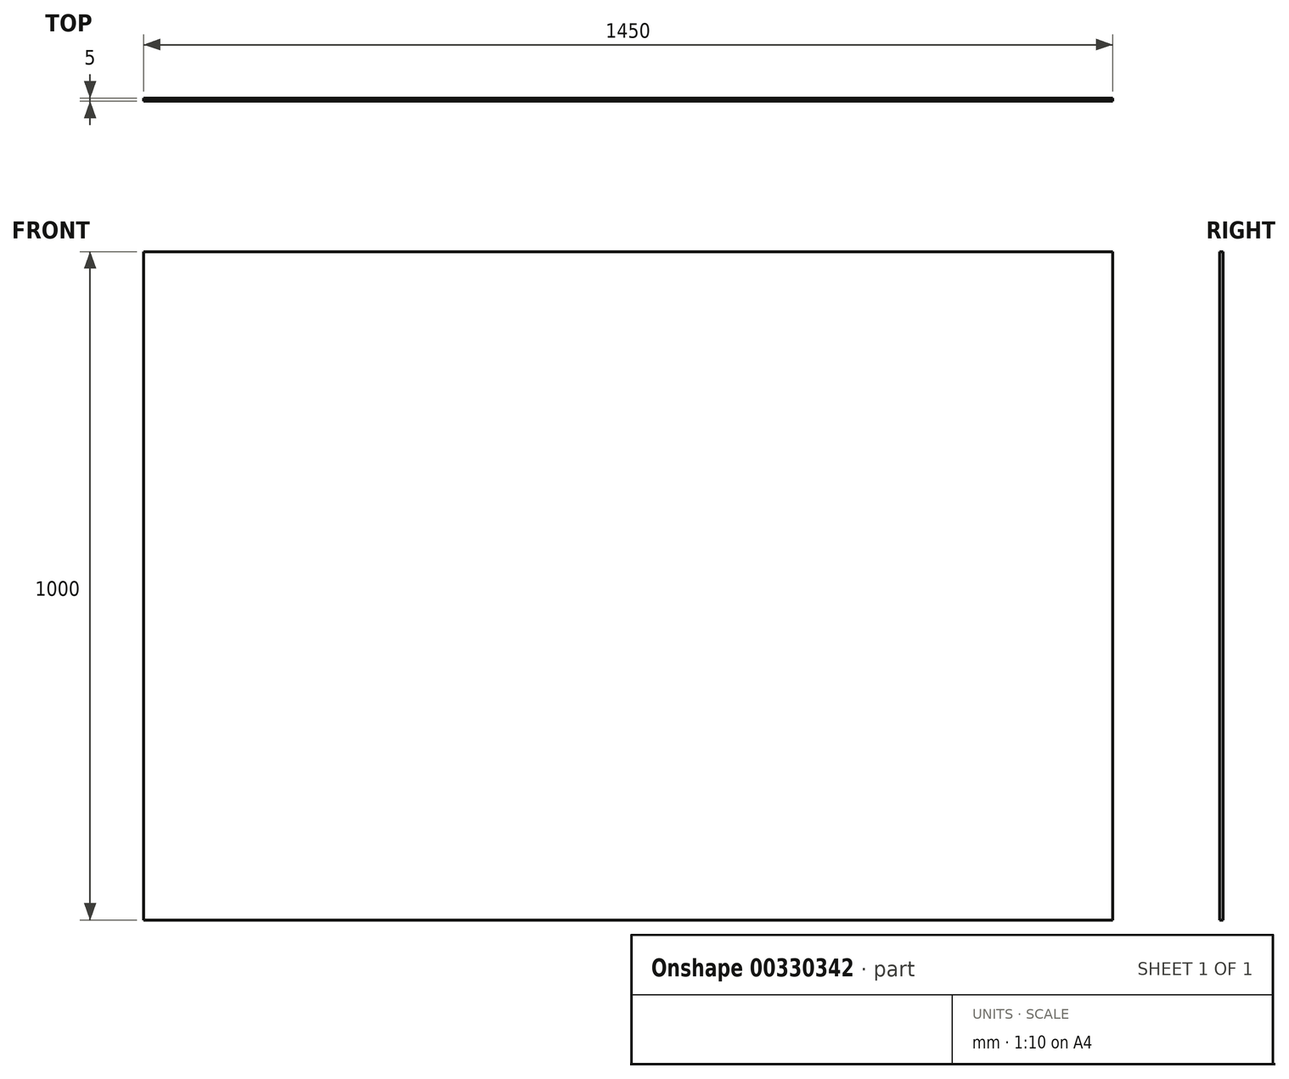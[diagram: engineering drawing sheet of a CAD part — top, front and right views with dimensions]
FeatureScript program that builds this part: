
annotation { "Feature Type Name" : "Feature", "Feature Type Description" : "" }
export const myFeature = defineFeature(function(context is Context, id is Id, definition is map)
    precondition{}
    {
        {
            var Q0;
            Q0=qCreatedBy(makeId("Front.planeOp"),FACE);
            var sketch = newSketch(context, id + "F0", { "sketchPlane" : qUnion([Q0])});
            skLineSegment(sketch, "E0.bottom", {"start": v(0, 0) * mm, "end": v(1450, 0) * mm});
            skLineSegment(sketch, "E0.top", {"start": v(0, 1000) * mm, "end": v(1450, 1000) * mm});
            skLineSegment(sketch, "E0.left", {"start": v(0, 0) * mm, "end": v(0, 1000) * mm});
            skLineSegment(sketch, "E0.right", {"start": v(1450, 0) * mm, "end": v(1450, 1000) * mm});
            skSolve(sketch);
        }
        {
            var Q0;
            Q0 = qSketchRegion(id + "F0", true);
            extrude(context, id + "F1", {"entities" : qUnion([Q0]), "depth" : 5 * mm, "offsetDistance" : 25 * mm});
        }
    });
